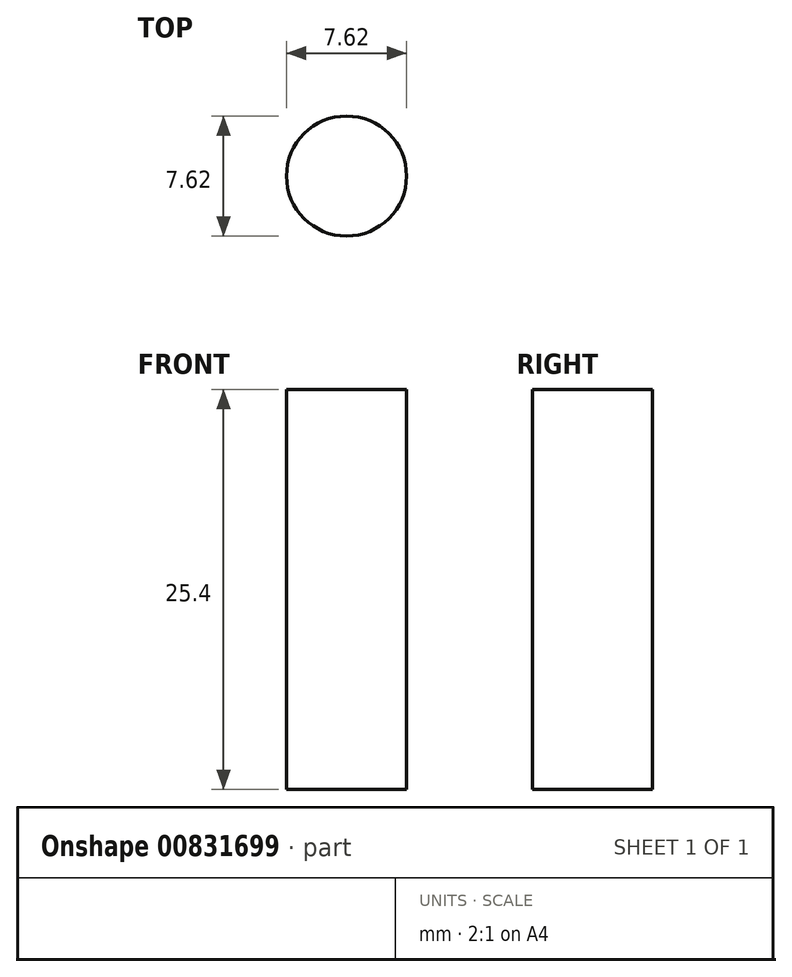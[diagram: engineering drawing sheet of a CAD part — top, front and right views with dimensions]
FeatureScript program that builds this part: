
annotation { "Feature Type Name" : "Feature", "Feature Type Description" : "" }
export const myFeature = defineFeature(function(context is Context, id is Id, definition is map)
    precondition{}
    {
        {
            var Q0;
            Q0=qCreatedBy(makeId("Front.planeOp"),FACE);
            var sketch = newSketch(context, id + "F0", { "sketchPlane" : qUnion([Q0])});
            skLineSegment(sketch, "E0.bottom", {"start": v(0, 0) * mm, "end": v(3.8, 0) * mm});
            skLineSegment(sketch, "E0.top", {"start": v(0, 25.4) * mm, "end": v(3.8, 25.4) * mm});
            skLineSegment(sketch, "E0.left", {"start": v(0, 0) * mm, "end": v(0, 25.4) * mm});
            skLineSegment(sketch, "E0.right", {"start": v(3.8, 0) * mm, "end": v(3.8, 25.4) * mm});
            skSolve(sketch);
        }
        {
            var Q0;
            Q0 = qSketchRegion(id + "F0", true);
            var Q1;
            Q1=sQuery(id+"F0.wireOp",EDGE,"E0.left");
            revolve(context, id + "F1", {"surfaceOperationType" : NewSurfaceOperationType.NEW, "entities" : qUnion([Q0]), "axis" : qUnion([Q1]), "revolveType" : RevolveType.FULL});
        }
    });
